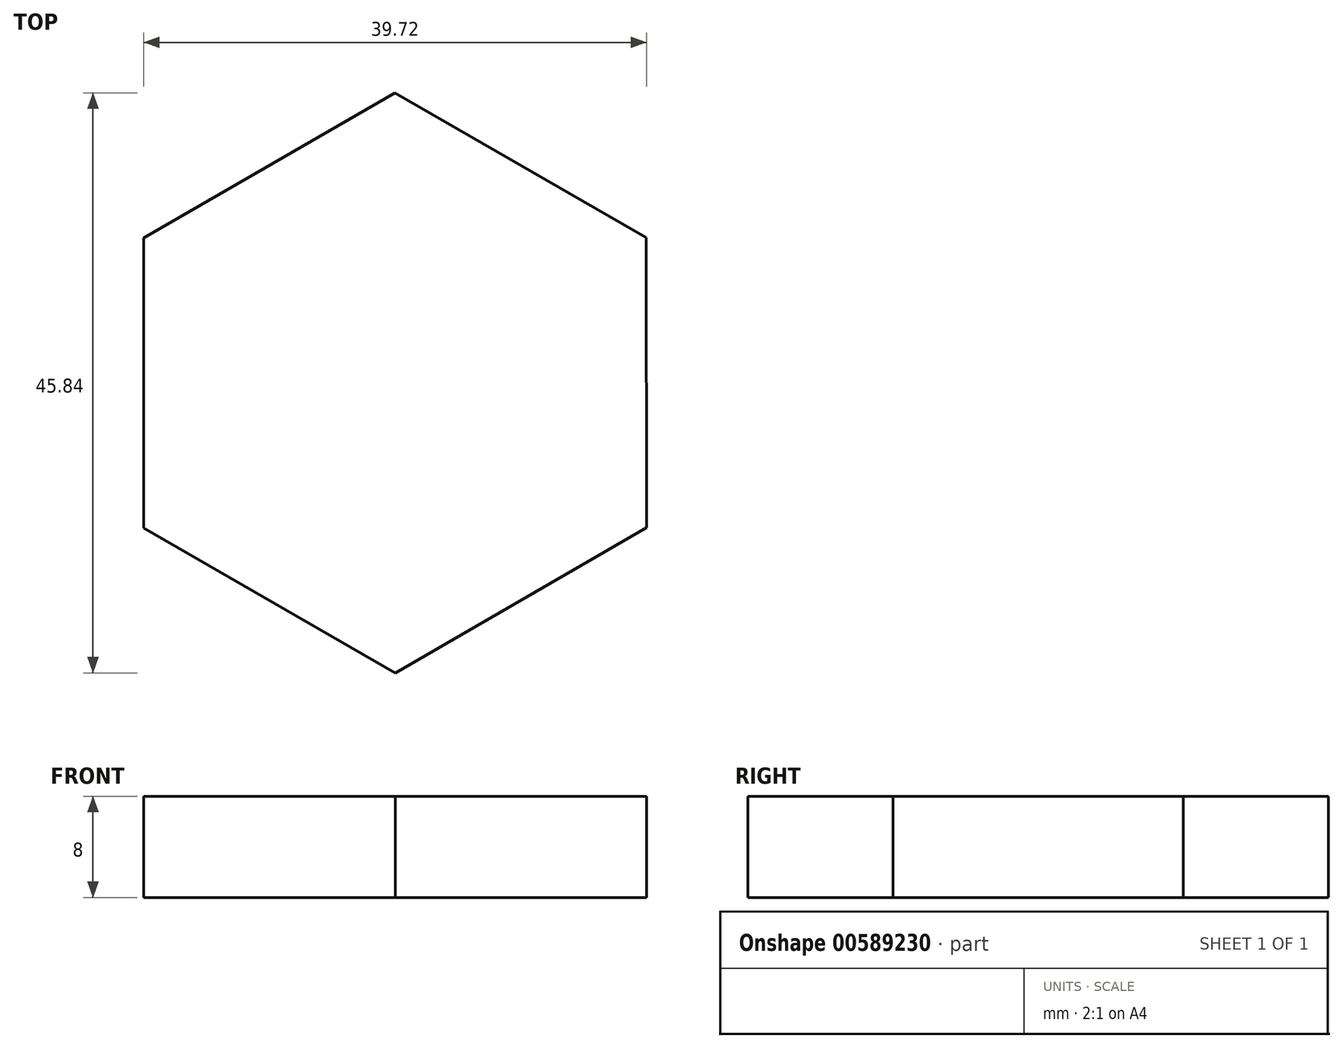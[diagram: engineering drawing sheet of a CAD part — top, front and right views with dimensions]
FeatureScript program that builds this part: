
annotation { "Feature Type Name" : "Feature", "Feature Type Description" : "" }
export const myFeature = defineFeature(function(context is Context, id is Id, definition is map)
    precondition{}
    {
        {
            var Q0;
            Q0=qCreatedBy(makeId("Top.planeOp"),FACE);
            var sketch = newSketch(context, id + "F0", { "sketchPlane" : qUnion([Q0])});
            skCircle(sketch, "E0", {"center": v(0, 0) * mm, "radius": 5.1 * mm});
            skSolve(sketch);
        }
        {
            var Q0;
            Q0=qCreatedBy(makeId("Top.planeOp"),FACE);
            var sketch = newSketch(context, id + "F1", { "sketchPlane" : qUnion([Q0])});
            skLineSegment(sketch, "E1.bottom", {"start": v(44.6, -32.2) * mm, "end": v(-44.6, -32.2) * mm});
            skLineSegment(sketch, "E1.top", {"start": v(44.6, 32.2) * mm, "end": v(-44.6, 32.2) * mm});
            skLineSegment(sketch, "E1.left", {"start": v(44.6, -32.2) * mm, "end": v(44.6, 32.2) * mm});
            skLineSegment(sketch, "E1.right", {"start": v(-44.6, -32.2) * mm, "end": v(-44.6, 32.2) * mm});
            skPoint(sketch, "E1.middle", {"position": v(0, 0) * mm});
            skSolve(sketch);
        }
        {
            var Q0;
            Q0=makeQuery(id+"F1.imprint","IMPRINT",FACE,{"disambiguationData":[TD([[makeQuery(id+"F1.imprint","IMPRINT",EDGE,{"derivedFrom":sQuery(id+"F1.wireOp",EDGE,"E1.bottom")}),-1.0]])]});
            var sketch = newSketch(context, id + "F2", { "sketchPlane" : qUnion([Q0])});
            skCircle(sketch, "E2.cCircle", {"center": v(0, 0) * mm, "radius": 19.85 * mm, "construction": true});
            skLineSegment(sketch, "E2.0", {"start": v(19.86, -11.44) * mm, "end": v(0.02, -22.92) * mm});
            skLineSegment(sketch, "E2.1", {"start": v(0.02, -22.92) * mm, "end": v(-19.84, -11.48) * mm});
            skLineSegment(sketch, "E2.2", {"start": v(-19.84, -11.48) * mm, "end": v(-19.86, 11.44) * mm});
            skLineSegment(sketch, "E2.3", {"start": v(-19.86, 11.44) * mm, "end": v(-0.02, 22.92) * mm});
            skLineSegment(sketch, "E2.4", {"start": v(-0.02, 22.92) * mm, "end": v(19.84, 11.48) * mm});
            skLineSegment(sketch, "E2.5", {"start": v(19.84, 11.48) * mm, "end": v(19.86, -11.44) * mm});
            skPoint(sketch, "E2.0.midPoint", {"position": v(9.94, -17.18) * mm});
            skSolve(sketch);
        }
        {
            var Q0;
            Q0=makeQuery(id+"F2.imprint","IMPRINT",FACE,{"disambiguationData":[TD([[makeQuery(id+"F2.imprint","IMPRINT",EDGE,{"derivedFrom":sQuery(id+"F2.wireOp",EDGE,"E2.0")}),-1.0]])]});
            extrude(context, id + "F3", {"entities" : qUnion([Q0]), "depth" : 8 * mm, "offsetDistance" : 25.4 * mm});
        }
        {
            var Q0;
            Q0 = qSketchRegion(id + "F0", true);
            extrude(context, id + "F4", {"entities" : qUnion([Q0]), "operationType" : NewBodyOperationType.REMOVE, "oppositeDirection" : true, "depth" : 25.4 * mm, "offsetDistance" : 25.4 * mm});
        }
        {
            var Q0;
            Q0 = qSketchRegion(id + "F0", true);
            extrude(context, id + "F5", {"entities" : qUnion([Q0]), "operationType" : NewBodyOperationType.REMOVE, "oppositeDirection" : true, "depth" : 25.4 * mm, "offsetDistance" : 25.4 * mm});
        }
    });
